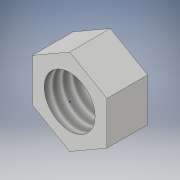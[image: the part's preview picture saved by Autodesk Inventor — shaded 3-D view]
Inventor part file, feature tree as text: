
AUTODESK INVENTOR PART (.ipt)
format: ipt  version: 2017 (Build 210142000, 142)  size: 104,448 bytes
history: native  units: in
note: dims shown in document units (in); Inventor stores cm internally (conversion verified against a paired STEP export)
features: sketch x2, extrude x1, thread x1
ambient origin geometry x8: Origin, YZ Plane, XZ Plane, XY Plane, X Axis, Y Axis, Z Axis, Center Point
bodies: Solid1 (feature_tree)
feature tree (4):
  extrude  "Extrusion1"  Depth=0.1in TaperAngle=0.0deg
  sketch  "Sketch2"
  thread  "Thread1"  [1 undecoded]
  sketch  "Sketch1"  dims[d0=0.125in d1=0.1in d2=0.0in d3=1.0in d4=0.0in]
note: 1 required parameter value undecoded (feature->parameter linkage not recoverable at this tier; creation-order binding heuristic only, values carry confidence <= 0.55)
